# Revit family: Haworth_BeHold_Accessory_WardrobeShelf
name_source: partatom
category: Furniture Systems
revit_build: Autodesk Revit 2018 (Build: 20170223_1515(x64)
units: mm (PartAtom-declared; Revit-internal decimal feet)

## family parameters
Always vertical = Yes
Cut with Voids When Loaded = No
OmniClass Number = 23.40.70.14.64.21
OmniClass Title = Systems Furniture
Part Type = Normal
Room Calculation Point = No
Round Connector Dimension = Use Diameter
Shared = No
Work Plane-Based = No

## types (1)
- 30d 24w
    Actual Depth = 30"
    Actual Height = 3/4"
    Actual Width = 24"
    Assembly Code = E2020200
    Case Thickness = 3/4"
    Custom Size = No
    Depth = 30"
    Description = Haworth - Be_Hold - Accessory - Wardrobe Shelf
    Double Control = Yes
    Manufacturer = Haworth
    Max. Depth = 30"
    Max. Width = 24"
    Min. Depth = 16"
    Min. Width = 12"
    Model = Haworth Be_Hold
    Revision Number = 1
    Shelf Edge Finish = Haworth _ Wood _ Maple H-AE
    Shelf Finish = Haworth _ Wood _ Maple H-AE
    Single Control = No
    Size = Verify Final Dim. w/ Haworth
    Standard Depths = 16, 18, 24, 30 in.
    Standard Widths = 12, 15, 24 in.
    Sustainability Info = https://www.haworth.com
    URL = http://www.haworth.com
    URL - Product = http://www.haworth.com
    Warranty = http://www.haworth.com
    Width = 24"

## geometry (parser evidence)
native form markers: Sweep x2
no freeform markers — native parametric forms only
